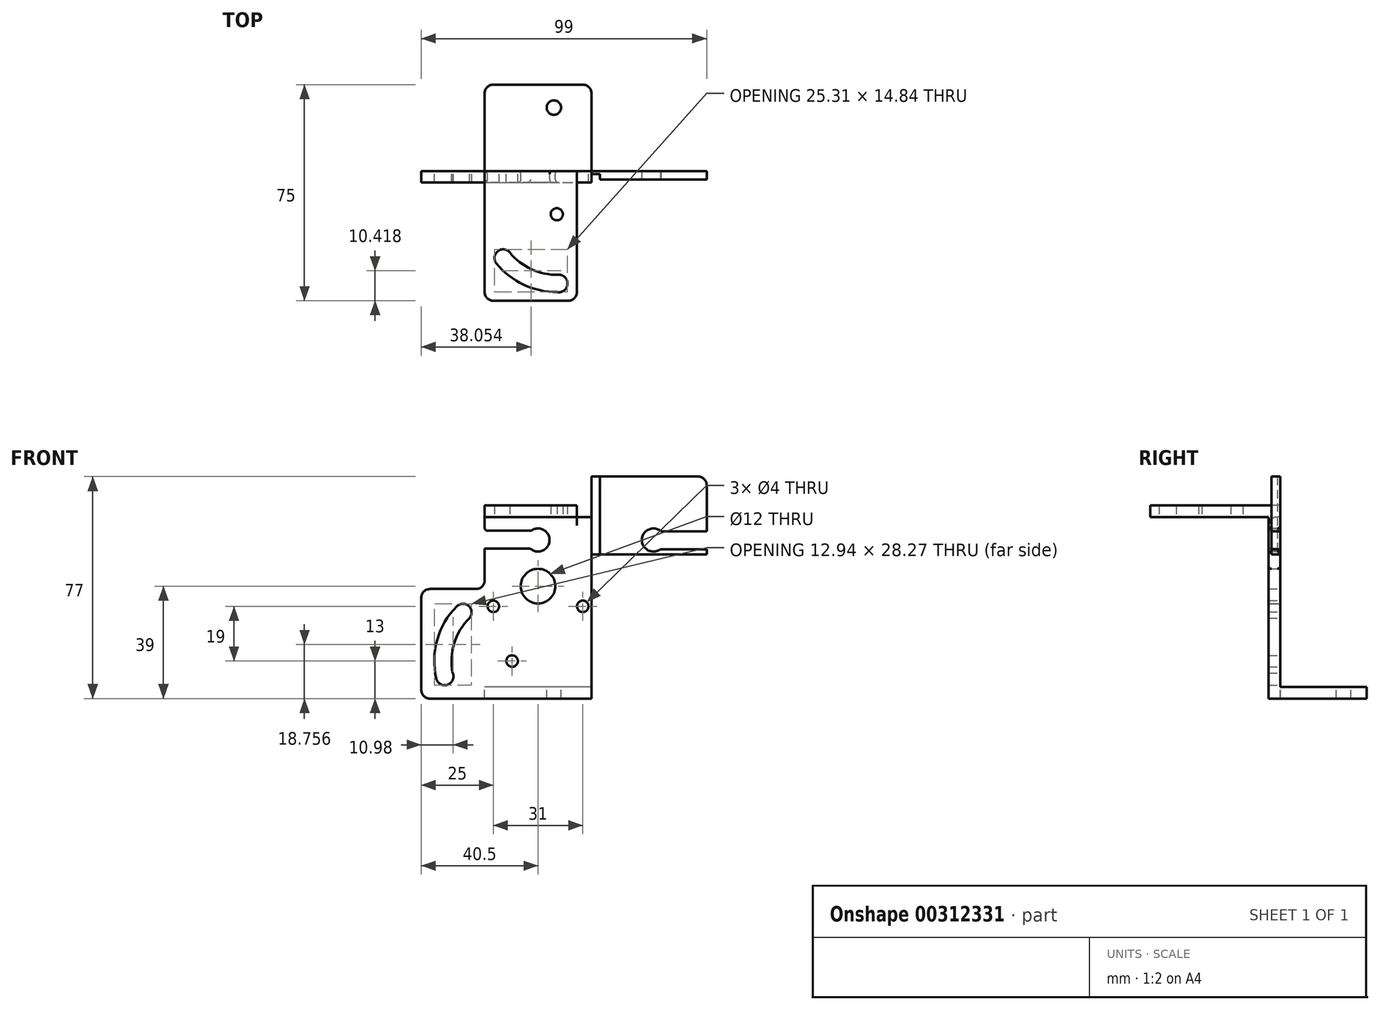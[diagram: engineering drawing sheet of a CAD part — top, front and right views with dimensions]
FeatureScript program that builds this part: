
annotation { "Feature Type Name" : "Feature", "Feature Type Description" : "" }
export const myFeature = defineFeature(function(context is Context, id is Id, definition is map)
    precondition{}
    {
        {
            var Q0;
            Q0=qCreatedBy(makeId("Front.planeOp"),FACE);
            var sketch = newSketch(context, id + "F0", { "sketchPlane" : qUnion([Q0])});
            skLineSegment(sketch, "E0", {"start": v(-18.5, -32) * mm, "end": v(18.5, -32) * mm});
            skLineSegment(sketch, "E1", {"start": v(18.5, -32) * mm, "end": v(18.5, 0) * mm});
            skCircle(sketch, "E2", {"center": v(0, 7) * mm, "radius": 6 * mm});
            skCircle(sketch, "E3", {"center": v(-15.5, 0) * mm, "radius": 2 * mm});
            skCircle(sketch, "E4", {"center": v(15.5, 0) * mm, "radius": 2 * mm});
            skLineSegment(sketch, "E5", {"start": v(-18.5, 31) * mm, "end": v(18.5, 31) * mm});
            skLineSegment(sketch, "E6", {"start": v(18.5, 31) * mm, "end": v(18.5, 0) * mm});
            skCircle(sketch, "E7", {"center": v(0, 23) * mm, "radius": 4 * mm});
            skArc(sketch, "E8", {"start": v(-18.5, 0) * mm, "mid": v(0, 18.5) * mm, "end": v(18.5, 0) * mm, "construction": true});
            skCircle(sketch, "E9", {"center": v(-9, -19) * mm, "radius": 2 * mm});
            skArc(sketch, "E10", {"start": v(-23.77, -4.08) * mm, "mid": v(-29.1, -12.9) * mm, "end": v(-29.58, -23.2) * mm});
            skArc(sketch, "E11", {"start": v(-28.18, 0) * mm, "mid": v(-34.97, -11.6) * mm, "end": v(-35.31, -25.05) * mm});
            skArc(sketch, "E12", {"start": v(-28.18, 0) * mm, "mid": v(-24, 0.1) * mm, "end": v(-23.77, -4.08) * mm});
            skArc(sketch, "E13", {"start": v(-35.31, -25.05) * mm, "mid": v(-31.44, -27.25) * mm, "end": v(-29.58, -23.2) * mm});
            skLineSegment(sketch, "E14", {"start": v(-18.5, 31) * mm, "end": v(-18.5, 6) * mm});
            skLineSegment(sketch, "E15", {"start": v(-18.5, 6) * mm, "end": v(-40.5, 6) * mm});
            skLineSegment(sketch, "E16", {"start": v(-40.5, 6) * mm, "end": v(-40.5, -32) * mm});
            skLineSegment(sketch, "E17", {"start": v(-40.5, -32) * mm, "end": v(-18.5, -32) * mm});
            skSolve(sketch);
        }
        {
            var Q0;
            Q0=qSketchRegion(id+"F0",true);
            extrude(context, id + "F1", {"entities" : qUnion([Q0]), "depth" : 4 * mm});
        }
        {
            var Q0;
            Q0=qCreatedBy(makeId("Top.planeOp"),FACE);
            var sketch = newSketch(context, id + "F2", { "sketchPlane" : qUnion([Q0])});
            skLineSegment(sketch, "E18", {"start": v(18.5, -1) * mm, "end": v(18.5, 0) * mm});
            skLineSegment(sketch, "E19", {"start": v(18.5, 0) * mm, "end": v(58.5, 0) * mm});
            skLineSegment(sketch, "E20", {"start": v(58.5, 0) * mm, "end": v(58.5, -3) * mm});
            skLineSegment(sketch, "E21", {"start": v(58.5, -3) * mm, "end": v(21.5, -3) * mm});
            skLineSegment(sketch, "E22", {"start": v(21.5, -3) * mm, "end": v(21.5, -1) * mm});
            skLineSegment(sketch, "E23", {"start": v(21.5, -1) * mm, "end": v(18.5, -1) * mm});
            skSolve(sketch);
        }
        {
            var Q0;
            Q0=qSketchRegion(id+"F2",true);
            extrude(context, id + "F3", {"entities" : qUnion([Q0]), "operationType" : NewBodyOperationType.ADD, "depth" : 45 * mm});
        }
        {
            var Q0;
            Q0=makeQuery(id+"F3.opExtrude","SWEPT_FACE",FACE,{"disambiguationData":[OSD([sQuery(id+"F2.wireOp",EDGE,"E21")])]});
            var sketch = newSketch(context, id + "F4", { "sketchPlane" : qUnion([Q0])});
            skCircle(sketch, "E24", {"center": v(40, 23) * mm, "radius": 4 * mm});
            skSolve(sketch);
        }
        {
            var Q0;
            Q0=qSketchRegion(id+"F4",true);
            extrude(context, id + "F5", {"entities" : qUnion([Q0]), "operationType" : NewBodyOperationType.REMOVE, "endBound" : BoundingType.THROUGH_ALL, "oppositeDirection" : true, "depth" : 25 * mm});
        }
        {
            var Q0;
            Q0=makeQuery(id+"F1.opExtrude","CAP_FACE",FACE,{"disambiguationData":[OSD([sQuery(id+"F0.wireOp",EDGE,"E0"),sQuery(id+"F0.wireOp",EDGE,"E1"),sQuery(id+"F0.wireOp",EDGE,"E2"),sQuery(id+"F0.wireOp",EDGE,"E3"),sQuery(id+"F0.wireOp",EDGE,"E4"),sQuery(id+"F0.wireOp",EDGE,"E5"),sQuery(id+"F0.wireOp",EDGE,"E6"),sQuery(id+"F0.wireOp",EDGE,"E7"),sQuery(id+"F0.wireOp",EDGE,"E9"),sQuery(id+"F0.wireOp",EDGE,"E10"),sQuery(id+"F0.wireOp",EDGE,"E11"),sQuery(id+"F0.wireOp",EDGE,"E12"),sQuery(id+"F0.wireOp",EDGE,"E13"),sQuery(id+"F0.wireOp",EDGE,"E14"),sQuery(id+"F0.wireOp",EDGE,"E15"),sQuery(id+"F0.wireOp",EDGE,"E16"),sQuery(id+"F0.wireOp",EDGE,"E17")])],"isStart":false});
            var sketch = newSketch(context, id + "F6", { "sketchPlane" : qUnion([Q0])});
            skLineSegment(sketch, "E25.bottom", {"start": v(-18.5, 26.2) * mm, "end": v(-0.5, 26.2) * mm});
            skLineSegment(sketch, "E25.top", {"start": v(-18.5, 20) * mm, "end": v(-0.5, 20) * mm});
            skLineSegment(sketch, "E25.left", {"start": v(-18.5, 26.2) * mm, "end": v(-18.5, 20) * mm});
            skLineSegment(sketch, "E25.right", {"start": v(-0.5, 26.2) * mm, "end": v(-0.5, 20) * mm});
            skLineSegment(sketch, "E26.bottom", {"start": v(58.5, 26) * mm, "end": v(40.5, 26) * mm});
            skLineSegment(sketch, "E26.top", {"start": v(58.5, 19.8) * mm, "end": v(40.5, 19.8) * mm});
            skLineSegment(sketch, "E26.left", {"start": v(58.5, 26) * mm, "end": v(58.5, 19.8) * mm});
            skLineSegment(sketch, "E26.right", {"start": v(40.5, 26) * mm, "end": v(40.5, 19.8) * mm});
            skLineSegment(sketch, "E27.bottom", {"start": v(58.5, 0) * mm, "end": v(18.5, 0) * mm});
            skLineSegment(sketch, "E27.top", {"start": v(58.5, 18) * mm, "end": v(18.5, 18) * mm});
            skLineSegment(sketch, "E27.left", {"start": v(58.5, 0) * mm, "end": v(58.5, 18) * mm});
            skLineSegment(sketch, "E27.right", {"start": v(18.5, 0) * mm, "end": v(18.5, 18) * mm});
            skSolve(sketch);
        }
        {
            var Q0;
            Q0=qSketchRegion(id+"F6",true);
            extrude(context, id + "F7", {"entities" : qUnion([Q0]), "operationType" : NewBodyOperationType.REMOVE, "endBound" : BoundingType.THROUGH_ALL, "oppositeDirection" : true, "depth" : 25 * mm});
        }
        {
            var Q0;
            Q0=makeQuery(id+"F3.boolean.opBoolean","MERGE",FACE,{"derivedFrom":[makeQuery(id+"F1.opExtrude","CAP_FACE",FACE,{"disambiguationData":[OSD([sQuery(id+"F0.wireOp",EDGE,"E0"),sQuery(id+"F0.wireOp",EDGE,"E1"),sQuery(id+"F0.wireOp",EDGE,"E2"),sQuery(id+"F0.wireOp",EDGE,"E3"),sQuery(id+"F0.wireOp",EDGE,"E4"),sQuery(id+"F0.wireOp",EDGE,"E5"),sQuery(id+"F0.wireOp",EDGE,"E6"),sQuery(id+"F0.wireOp",EDGE,"E7"),sQuery(id+"F0.wireOp",EDGE,"E9"),sQuery(id+"F0.wireOp",EDGE,"E10"),sQuery(id+"F0.wireOp",EDGE,"E11"),sQuery(id+"F0.wireOp",EDGE,"E12"),sQuery(id+"F0.wireOp",EDGE,"E13"),sQuery(id+"F0.wireOp",EDGE,"E14"),sQuery(id+"F0.wireOp",EDGE,"E15"),sQuery(id+"F0.wireOp",EDGE,"E16"),sQuery(id+"F0.wireOp",EDGE,"E17")])],"isStart":true}),makeQuery(id+"F3.opExtrude","SWEPT_FACE",FACE,{"disambiguationData":[OSD([sQuery(id+"F2.wireOp",EDGE,"E19")])]})]});
            var sketch = newSketch(context, id + "F8", { "sketchPlane" : qUnion([Q0])});
            skLineSegment(sketch, "E28.bottom", {"start": v(-18.5, -32) * mm, "end": v(18.5, -32) * mm});
            skLineSegment(sketch, "E28.top", {"start": v(-18.5, -28) * mm, "end": v(18.5, -28) * mm});
            skLineSegment(sketch, "E28.left", {"start": v(-18.5, -32) * mm, "end": v(-18.5, -28) * mm});
            skLineSegment(sketch, "E28.right", {"start": v(18.5, -32) * mm, "end": v(18.5, -28) * mm});
            skSolve(sketch);
        }
        {
            var Q0;
            Q0=qSketchRegion(id+"F8",true);
            extrude(context, id + "F9", {"entities" : qUnion([Q0]), "operationType" : NewBodyOperationType.ADD, "depth" : 30 * mm});
        }
        {
            var Q0;
            Q0=makeQuery(id+"F9.opExtrude","SWEPT_FACE",FACE,{"disambiguationData":[OSD([sQuery(id+"F8.wireOp",EDGE,"E28.top")])]});
            var sketch = newSketch(context, id + "F10", { "sketchPlane" : qUnion([Q0])});
            skCircle(sketch, "E29", {"center": v(5.5, 22) * mm, "radius": 2.5 * mm});
            skSolve(sketch);
        }
        {
            var Q0;
            Q0=qSketchRegion(id+"F10",true);
            extrude(context, id + "F11", {"entities" : qUnion([Q0]), "operationType" : NewBodyOperationType.REMOVE, "endBound" : BoundingType.THROUGH_ALL, "oppositeDirection" : true, "depth" : 25 * mm});
        }
        {
            var Q0;
            Q0=makeQuery(id+"F1.opExtrude","SWEPT_FACE",FACE,{"disambiguationData":[OSD([sQuery(id+"F0.wireOp",EDGE,"E5")])]});
            var sketch = newSketch(context, id + "F12", { "sketchPlane" : qUnion([Q0])});
            skLineSegment(sketch, "E30.bottom", {"start": v(-18.5, 0) * mm, "end": v(13.5, 0) * mm});
            skLineSegment(sketch, "E30.top", {"start": v(-18.5, -45) * mm, "end": v(13.5, -45) * mm});
            skLineSegment(sketch, "E30.left", {"start": v(-18.5, 0) * mm, "end": v(-18.5, -45) * mm});
            skLineSegment(sketch, "E30.right", {"start": v(13.5, 0) * mm, "end": v(13.5, -45) * mm});
            skCircle(sketch, "E31", {"center": v(6.5, -15) * mm, "radius": 2.1 * mm});
            skArc(sketch, "E32", {"start": v(-14.45, -32.04) * mm, "mid": v(-5.04, -39.4) * mm, "end": v(6.62, -42) * mm});
            skArc(sketch, "E33", {"start": v(-9.76, -28.29) * mm, "mid": v(-2.23, -34.1) * mm, "end": v(7.1, -36) * mm});
            skArc(sketch, "E34", {"start": v(-14.45, -32.04) * mm, "mid": v(-14, -27.8) * mm, "end": v(-9.76, -28.29) * mm});
            skArc(sketch, "E35", {"start": v(7.1, -36) * mm, "mid": v(10.2, -39.26) * mm, "end": v(6.62, -42) * mm});
            skSolve(sketch);
        }
        {
            var Q0;
            Q0=qSketchRegion(id+"F12",true);
            extrude(context, id + "F13", {"entities" : qUnion([Q0]), "operationType" : NewBodyOperationType.ADD, "depth" : 4 * mm});
        }
        {
            var Q0;
            Q0=makeQuery(id+"F1.opExtrude","SWEPT_FACE",FACE,{"disambiguationData":[OSD([sQuery(id+"F0.wireOp",EDGE,"E2")])]});
            var Q1;
            Q1=makeQuery(id+"F1.opExtrude","SWEPT_FACE",FACE,{"disambiguationData":[OSD([sQuery(id+"F0.wireOp",EDGE,"E7")])]});
            var Q2;
            Q2=makeQuery(id+"F7.boolean.opBoolean","COPY",FACE,{"derivedFrom":makeQuery(id+"F7.opExtrude","SWEPT_FACE",FACE,{"disambiguationData":[OSD([sQuery(id+"F6.wireOp",EDGE,"E25.bottom")])]})});
            var Q3;
            Q3=makeQuery(id+"F7.boolean.opBoolean","INTERSECT",EDGE,{"derivedFrom":[makeQuery(id+"F3.boolean.opBoolean","MERGE",FACE,{"derivedFrom":[makeQuery(id+"F1.opExtrude","CAP_FACE",FACE,{"disambiguationData":[OSD([sQuery(id+"F0.wireOp",EDGE,"E0"),sQuery(id+"F0.wireOp",EDGE,"E1"),sQuery(id+"F0.wireOp",EDGE,"E2"),sQuery(id+"F0.wireOp",EDGE,"E3"),sQuery(id+"F0.wireOp",EDGE,"E4"),sQuery(id+"F0.wireOp",EDGE,"E5"),sQuery(id+"F0.wireOp",EDGE,"E6"),sQuery(id+"F0.wireOp",EDGE,"E7"),sQuery(id+"F0.wireOp",EDGE,"E9"),sQuery(id+"F0.wireOp",EDGE,"E10"),sQuery(id+"F0.wireOp",EDGE,"E11"),sQuery(id+"F0.wireOp",EDGE,"E12"),sQuery(id+"F0.wireOp",EDGE,"E13"),sQuery(id+"F0.wireOp",EDGE,"E14"),sQuery(id+"F0.wireOp",EDGE,"E15"),sQuery(id+"F0.wireOp",EDGE,"E16"),sQuery(id+"F0.wireOp",EDGE,"E17")])],"isStart":true}),makeQuery(id+"F3.opExtrude","SWEPT_FACE",FACE,{"disambiguationData":[OSD([sQuery(id+"F2.wireOp",EDGE,"E19")])]})]}),makeQuery(id+"F7.opExtrude","SWEPT_FACE",FACE,{"disambiguationData":[OSD([sQuery(id+"F6.wireOp",EDGE,"E25.top")])]})]});
            fillet(context, id + "F14", {"entities" : qUnion([Q0, Q1, Q2, Q3]), "radius" : 1 * mm, "tangentPropagation" : true, "allowEdgeOverflow" : false});
        }
        {
            var Q0;
            Q0=makeQuery(id+"F9.opExtrude","CAP_EDGE",EDGE,{"disambiguationData":[OSD([sQuery(id+"F8.wireOp",EDGE,"E28.top")])],"isStart":true});
            var Q1;
            Q1=makeQuery(id+"F1.opExtrude","SWEPT_EDGE",EDGE,{"disambiguationData":[OSD([sQuery(id+"F0.wireOp",EDGE,"E15"),sQuery(id+"F0.wireOp",EDGE,"E16")])]});
            var Q2;
            Q2=makeQuery(id+"F1.opExtrude","SWEPT_EDGE",EDGE,{"disambiguationData":[OSD([sQuery(id+"F0.wireOp",EDGE,"E16"),sQuery(id+"F0.wireOp",EDGE,"E17")])]});
            var Q3;
            Q3=makeQuery(id+"F9.opExtrude","CAP_EDGE",EDGE,{"disambiguationData":[OSD([sQuery(id+"F8.wireOp",EDGE,"E28.left")])],"isStart":false});
            var Q4;
            Q4=makeQuery(id+"F9.opExtrude","CAP_EDGE",EDGE,{"disambiguationData":[OSD([sQuery(id+"F8.wireOp",EDGE,"E28.right")])],"isStart":false});
            var Q5;
            Q5=makeQuery(id+"F3.opExtrude","CAP_EDGE",EDGE,{"disambiguationData":[OSD([sQuery(id+"F2.wireOp",EDGE,"E20")])],"isStart":false});
            var Q6;
            Q6=makeQuery(id+"F13.opExtrude","SWEPT_EDGE",EDGE,{"disambiguationData":[OSD([sQuery(id+"F12.wireOp",EDGE,"E30.top"),sQuery(id+"F12.wireOp",EDGE,"E30.left")])]});
            var Q7;
            Q7=makeQuery(id+"F13.opExtrude","SWEPT_EDGE",EDGE,{"disambiguationData":[OSD([sQuery(id+"F12.wireOp",EDGE,"E30.top"),sQuery(id+"F12.wireOp",EDGE,"E30.right")])]});
            fillet(context, id + "F15", {"entities" : qUnion([Q0, Q1, Q2, Q3, Q4, Q5, Q6, Q7]), "radius" : 3 * mm, "tangentPropagation" : true, "allowEdgeOverflow" : false});
        }
        {
            var Q0;
            {var subQ0=sQuery(id+"F0.wireOp",EDGE,"E5");Q0=makeQuery(id+"F13.boolean.opBoolean","SPLIT",EDGE,{"disambiguationData":[topologyDisambiguationEdgeConnected([makeQuery(id+"F13.opExtrude","CAP_FACE",FACE,{"disambiguationData":[OSD([sQuery(id+"F12.wireOp",EDGE,"E30.bottom"),sQuery(id+"F12.wireOp",EDGE,"E30.top"),sQuery(id+"F12.wireOp",EDGE,"E30.left"),sQuery(id+"F12.wireOp",EDGE,"E30.right"),sQuery(id+"F12.wireOp",EDGE,"E31"),sQuery(id+"F12.wireOp",EDGE,"E32"),sQuery(id+"F12.wireOp",EDGE,"E33"),sQuery(id+"F12.wireOp",EDGE,"E34"),sQuery(id+"F12.wireOp",EDGE,"E35")])],"isStart":true})])],"derivedFrom":makeQuery(id+"F1.opExtrude","CAP_EDGE",EDGE,{"disambiguationData":[OSD([subQ0])],"isStart":false})});}
            var Q1;
            Q1=makeQuery(id+"F1.opExtrude","SWEPT_EDGE",EDGE,{"disambiguationData":[OSD([sQuery(id+"F0.wireOp",EDGE,"E14"),sQuery(id+"F0.wireOp",EDGE,"E15")])]});
            fillet(context, id + "F16", {"entities" : qUnion([Q0, Q1]), "radius" : 3 * mm, "tangentPropagation" : true, "allowEdgeOverflow" : false});
        }
    });
